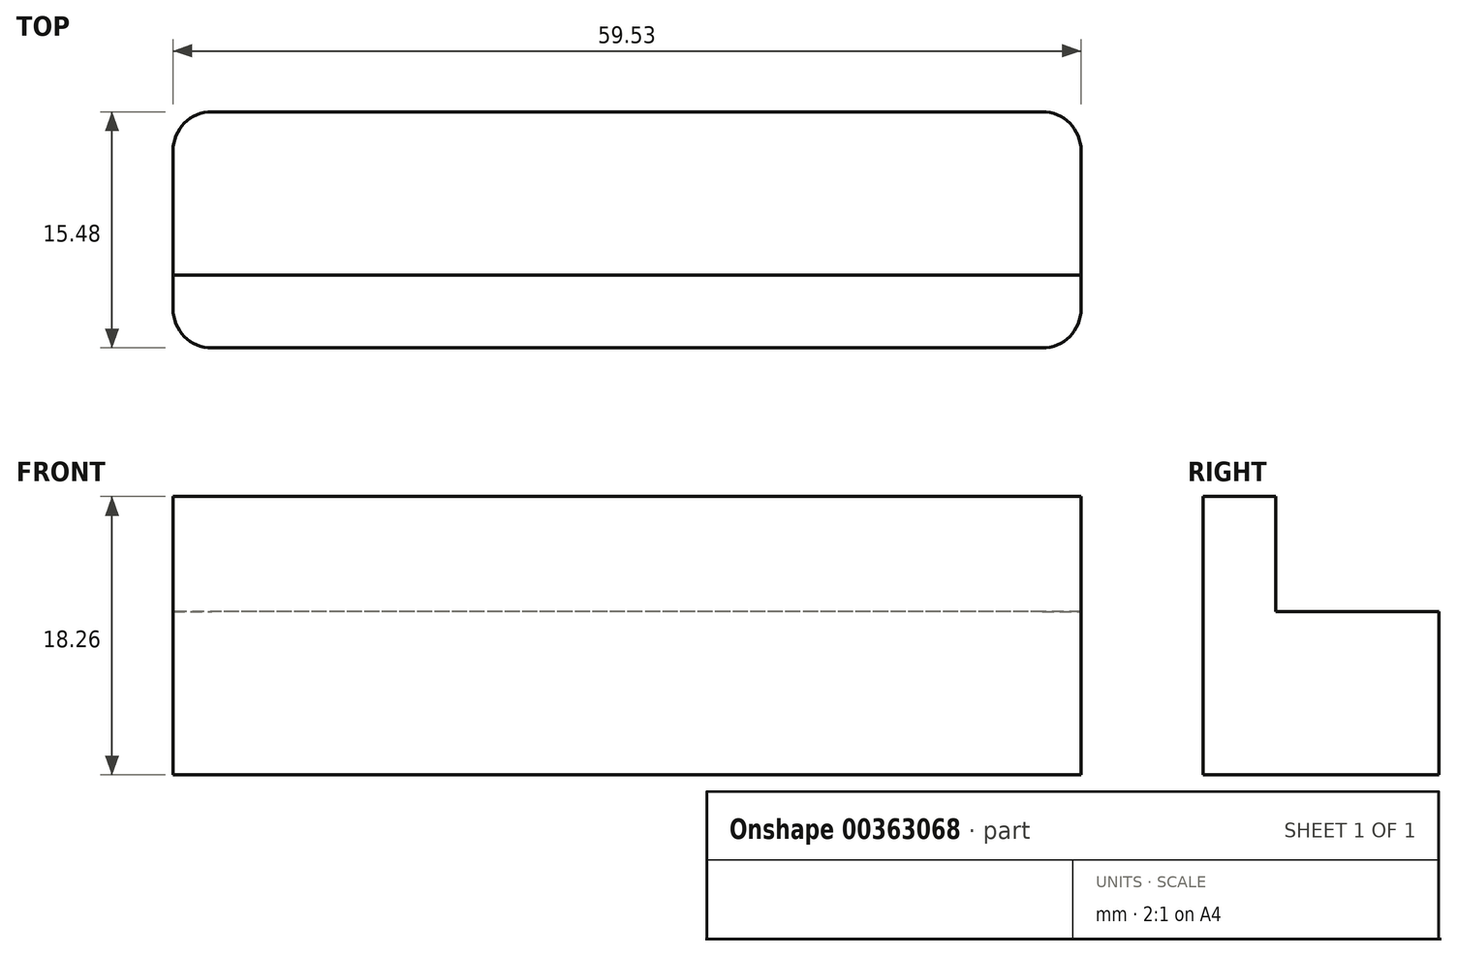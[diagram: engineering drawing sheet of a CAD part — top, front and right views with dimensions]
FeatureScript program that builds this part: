
annotation { "Feature Type Name" : "Feature", "Feature Type Description" : "" }
export const myFeature = defineFeature(function(context is Context, id is Id, definition is map)
    precondition{}
    {
        {
            var Q0;
            Q0=qCreatedBy(makeId("Right.planeOp"),FACE);
            var sketch = newSketch(context, id + "F0", { "sketchPlane" : qUnion([Q0])});
            skLineSegment(sketch, "E0", {"start": v(0, 0) * mm, "end": v(15.48, 0) * mm});
            skLineSegment(sketch, "E1", {"start": v(15.48, 0) * mm, "end": v(15.48, 10.72) * mm});
            skLineSegment(sketch, "E2", {"start": v(15.48, 10.72) * mm, "end": v(4.76, 10.72) * mm});
            skLineSegment(sketch, "E3", {"start": v(4.76, 10.72) * mm, "end": v(4.76, 18.26) * mm});
            skLineSegment(sketch, "E4", {"start": v(4.76, 18.26) * mm, "end": v(0, 18.26) * mm});
            skLineSegment(sketch, "E5", {"start": v(0, 18.26) * mm, "end": v(0, 0) * mm});
            skSolve(sketch);
        }
        {
            var Q0;
            Q0=makeQuery(id+"F0.imprint","IMPRINT",FACE,{"disambiguationData":[TD([[makeQuery(id+"F0.imprint","IMPRINT",EDGE,{"derivedFrom":sQuery(id+"F0.wireOp",EDGE,"E0")}),1.0]])]});
            extrude(context, id + "F1", {"entities" : qUnion([Q0]), "depth" : 59.53 * mm});
        }
        {
            var Q0;
            Q0=makeQuery(id+"F1.opExtrude","CAP_EDGE",EDGE,{"disambiguationData":[OSD([sQuery(id+"F0.wireOp",EDGE,"E1")])],"isStart":true});
            var Q1;
            Q1=makeQuery(id+"F1.opExtrude","CAP_EDGE",EDGE,{"disambiguationData":[OSD([sQuery(id+"F0.wireOp",EDGE,"E5")])],"isStart":true});
            var Q2;
            Q2=makeQuery(id+"F1.opExtrude","CAP_EDGE",EDGE,{"disambiguationData":[OSD([sQuery(id+"F0.wireOp",EDGE,"E1")])],"isStart":false});
            var Q3;
            Q3=makeQuery(id+"F1.opExtrude","CAP_EDGE",EDGE,{"disambiguationData":[OSD([sQuery(id+"F0.wireOp",EDGE,"E5")])],"isStart":false});
            fillet(context, id + "F2", {"entities" : qUnion([Q0, Q1, Q2, Q3]), "radius" : 2.54 * mm, "tangentPropagation" : true, "allowEdgeOverflow" : false});
        }
    });
